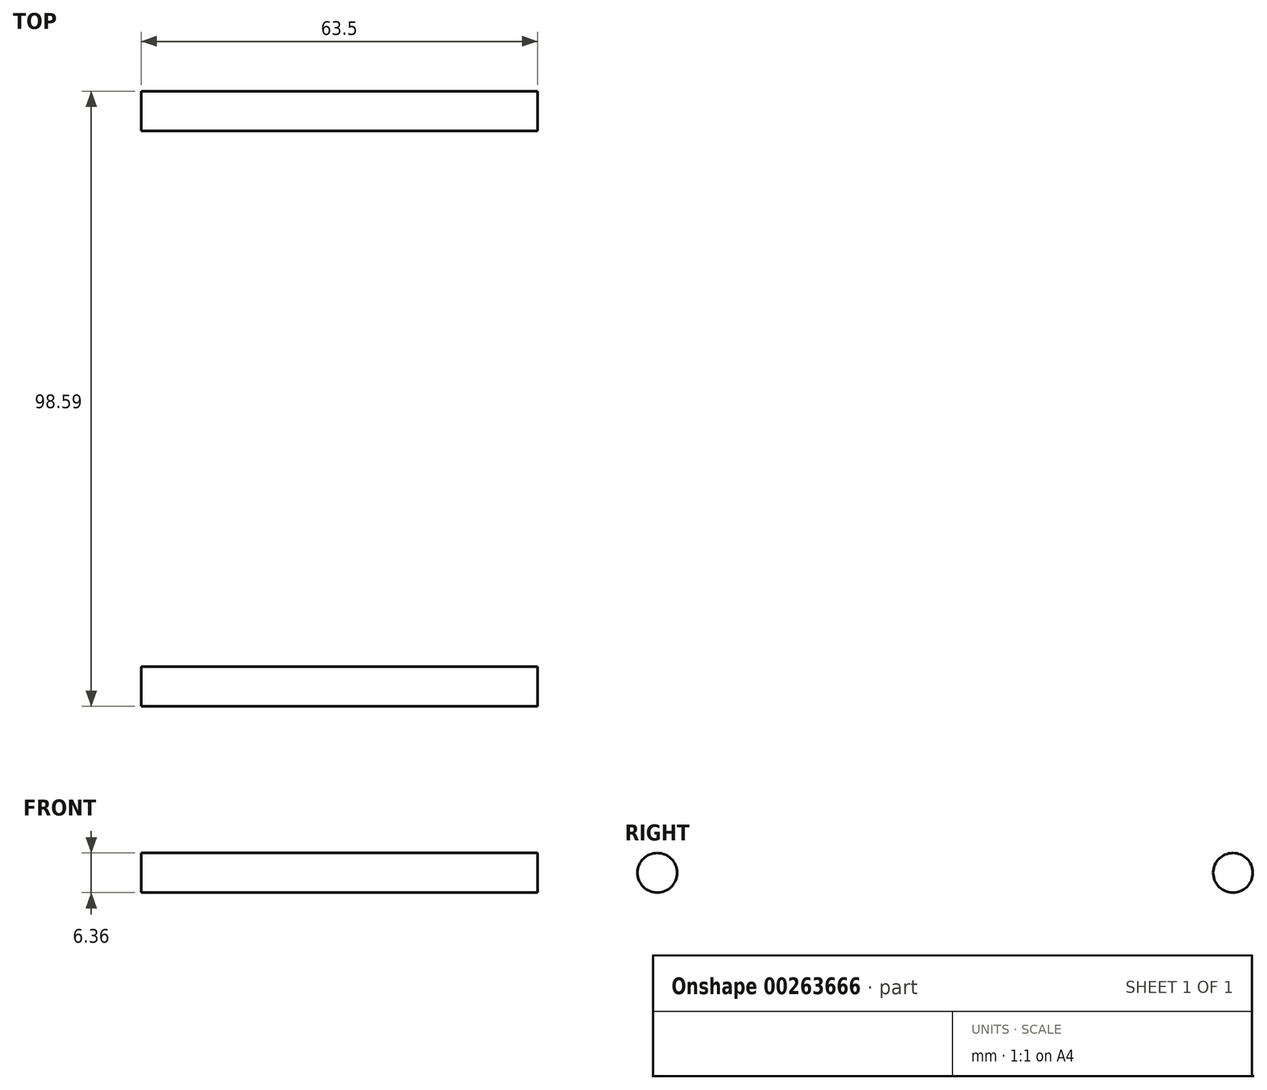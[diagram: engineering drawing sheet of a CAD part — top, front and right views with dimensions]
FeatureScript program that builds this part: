
annotation { "Feature Type Name" : "Feature", "Feature Type Description" : "" }
export const myFeature = defineFeature(function(context is Context, id is Id, definition is map)
    precondition{}
    {
        {
            var Q0;
            Q0=qCreatedBy(makeId("Right.planeOp"),FACE);
            var sketch = newSketch(context, id + "F0", { "sketchPlane" : qUnion([Q0])});
            skCircle(sketch, "E0", {"center": v(53.86, 0) * mm, "radius": 3.18 * mm});
            skCircle(sketch, "E1", {"center": v(-38.38, 0) * mm, "radius": 3.18 * mm});
            skSolve(sketch);
        }
        {
            var Q0;
            Q0=makeQuery(id+"F0.imprint","IMPRINT",FACE,{"disambiguationData":[TD([[makeQuery(id+"F0.imprint","IMPRINT",EDGE,{"derivedFrom":sQuery(id+"F0.wireOp",EDGE,"E1")}),1.0]])]});
            extrude(context, id + "F1", {"entities" : qUnion([Q0]), "depth" : 63.5 * mm});
        }
        {
            var Q0;
            Q0=makeQuery(id+"F0.imprint","IMPRINT",FACE,{"disambiguationData":[TD([[makeQuery(id+"F0.imprint","IMPRINT",EDGE,{"derivedFrom":sQuery(id+"F0.wireOp",EDGE,"E0")}),1.0]])]});
            extrude(context, id + "F2", {"entities" : qUnion([Q0]), "depth" : 63.5 * mm});
        }
    });
